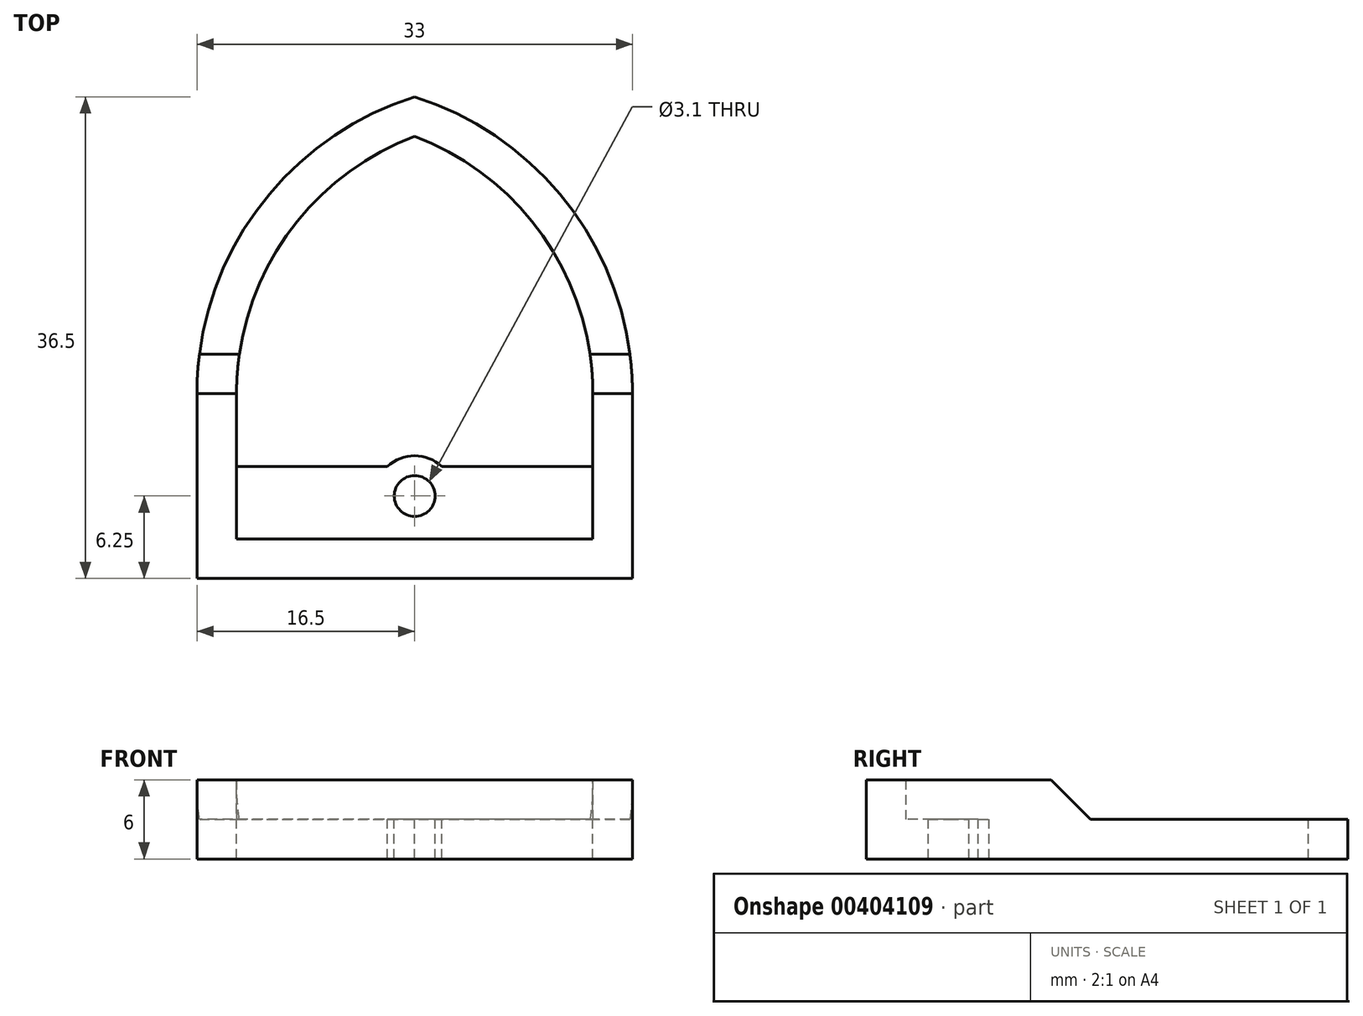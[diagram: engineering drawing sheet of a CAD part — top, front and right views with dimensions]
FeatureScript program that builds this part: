
annotation { "Feature Type Name" : "Feature", "Feature Type Description" : "" }
export const myFeature = defineFeature(function(context is Context, id is Id, definition is map)
    precondition{}
    {
        {
            var Q0;
            Q0=qCreatedBy(makeId("Top.planeOp"),FACE);
            var sketch = newSketch(context, id + "F0", { "sketchPlane" : qUnion([Q0])});
            skLineSegment(sketch, "E0", {"start": v(-16.5, -8.5) * mm, "end": v(16.5, -8.5) * mm});
            skLineSegment(sketch, "E1", {"start": v(16.5, -8.5) * mm, "end": v(16.5, 5.5) * mm});
            skLineSegment(sketch, "E2", {"start": v(-16.5, -8.5) * mm, "end": v(-16.5, 5.5) * mm});
            skArc(sketch, "E3", {"start": v(0, 28) * mm, "mid": v(-11.93, 19.45) * mm, "end": v(-16.5, 5.5) * mm});
            skArc(sketch, "E4", {"start": v(16.5, 5.5) * mm, "mid": v(11.93, 19.45) * mm, "end": v(0, 28) * mm});
            skPoint(sketch, "E5", {"position": v(0, -8.5) * mm});
            skLineSegment(sketch, "E6", {"start": v(13.5, 0) * mm, "end": v(13.5, 5.5) * mm});
            skLineSegment(sketch, "E7", {"start": v(-13.5, 0) * mm, "end": v(-13.5, 5.5) * mm});
            skArc(sketch, "E8", {"start": v(0, 25) * mm, "mid": v(-9.8, 17.36) * mm, "end": v(-13.5, 5.5) * mm});
            skArc(sketch, "E9", {"start": v(13.5, 5.5) * mm, "mid": v(9.8, 17.36) * mm, "end": v(0, 25) * mm});
            skPoint(sketch, "E10", {"position": v(0, 0) * mm});
            skCircle(sketch, "E11", {"center": v(0, -2.25) * mm, "radius": 1.55 * mm});
            skLineSegment(sketch, "E12", {"start": v(-13.5, 0) * mm, "end": v(-2.06, 0) * mm});
            skLineSegment(sketch, "E13", {"start": v(13.5, 0) * mm, "end": v(2.06, 0) * mm});
            skArc(sketch, "E14", {"start": v(2.06, 0) * mm, "mid": v(0, 0.8) * mm, "end": v(-2.06, 0) * mm});
            skSolve(sketch);
        }
        {
            var Q0;
            Q0=makeQuery(id+"F0.imprint","IMPRINT",FACE,{"disambiguationData":[TD([[makeQuery(id+"F0.imprint","IMPRINT",EDGE,{"derivedFrom":sQuery(id+"F0.wireOp",EDGE,"E0")}),1.0]])]});
            extrude(context, id + "F1", {"entities" : qUnion([Q0]), "oppositeDirection" : true, "depth" : 3 * mm});
        }
        {
            var Q0;
            Q0=qCreatedBy(makeId("Top.planeOp"),FACE);
            var sketch = newSketch(context, id + "F2", { "sketchPlane" : qUnion([Q0])});
            skLineSegment(sketch, "E15", {"start": v(-16.5, -8.5) * mm, "end": v(-16.5, 5.5) * mm});
            skLineSegment(sketch, "E16", {"start": v(-16.5, 5.5) * mm, "end": v(-13.5, 5.5) * mm});
            skLineSegment(sketch, "E17", {"start": v(-13.5, 5.5) * mm, "end": v(-13.5, -5.5) * mm});
            skLineSegment(sketch, "E18", {"start": v(-13.5, -5.5) * mm, "end": v(13.5, -5.5) * mm});
            skLineSegment(sketch, "E19", {"start": v(13.5, -5.5) * mm, "end": v(13.5, 5.5) * mm});
            skLineSegment(sketch, "E20", {"start": v(13.5, 5.5) * mm, "end": v(16.5, 5.5) * mm});
            skLineSegment(sketch, "E21", {"start": v(16.5, 5.5) * mm, "end": v(16.5, -8.5) * mm});
            skLineSegment(sketch, "E22", {"start": v(16.5, -8.5) * mm, "end": v(-16.5, -8.5) * mm});
            skSolve(sketch);
        }
        {
            var Q0;
            Q0=makeQuery(id+"F2.imprint","IMPRINT",FACE,{"disambiguationData":[TD([[makeQuery(id+"F2.imprint","IMPRINT",EDGE,{"derivedFrom":sQuery(id+"F2.wireOp",EDGE,"E15")}),-1.0]])]});
            extrude(context, id + "F3", {"entities" : qUnion([Q0]), "operationType" : NewBodyOperationType.ADD, "depth" : 3 * mm});
        }
        {
            var Q0;
            Q0=makeQuery(id+"F3.opExtrude","CAP_EDGE",EDGE,{"disambiguationData":[OSD([sQuery(id+"F2.wireOp",EDGE,"E16")])],"isStart":true});
            var Q1;
            Q1=makeQuery(id+"F3.opExtrude","CAP_EDGE",EDGE,{"disambiguationData":[OSD([sQuery(id+"F2.wireOp",EDGE,"E20")])],"isStart":true});
            chamfer(context, id + "F4", {"entities" : qUnion([Q0, Q1]), "width" : 3 * mm, "tangentPropagation" : true});
        }
    });
